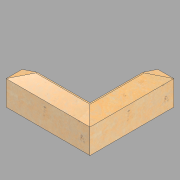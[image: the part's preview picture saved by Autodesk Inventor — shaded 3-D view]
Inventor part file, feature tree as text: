
AUTODESK INVENTOR PART (.ipt)
format: ipt  version: 2022.2 (Build 262287010, 287A)  size: 155,648 bytes
history: native  units: in
note: dims shown in document units (in); Inventor stores cm internally (conversion verified against a paired STEP export)
features: sketch x5, extrude x3, sweep x1
ambient origin geometry x8: Origin, YZ Plane, XZ Plane, XY Plane, X Axis, Y Axis, Z Axis, Center Point
bodies: Solid1 (feature_tree)
feature tree (9):
  extrude  "Extrusion1"  Depth=27.5in
  sweep  "Sweep1"
  extrude  "Extrusion2"  Depth=34.0in
  extrude  "Extrusion3"  Depth=12.0in
  sketch  "Sketch1"  dims[d1=27.5in d2=27.5in]
  sketch  "Sketch2"  dims[d3=6.5in d4=6.5in]
  sketch  "3D Sketch1"
  sketch  "Sketch3"  dims[d5=34.0in d6=34.0in]
  sketch  "Sketch4"  dims[d7=12.0in d8=0.0in d9=0.5in d10=2.0in d11=0.0in d12=0.0in d13=6.0in d14=2.0in d15=0.0in d16=0.0in d17=6.0in d18=2.0in d19=0.0in d20=0.0in]
